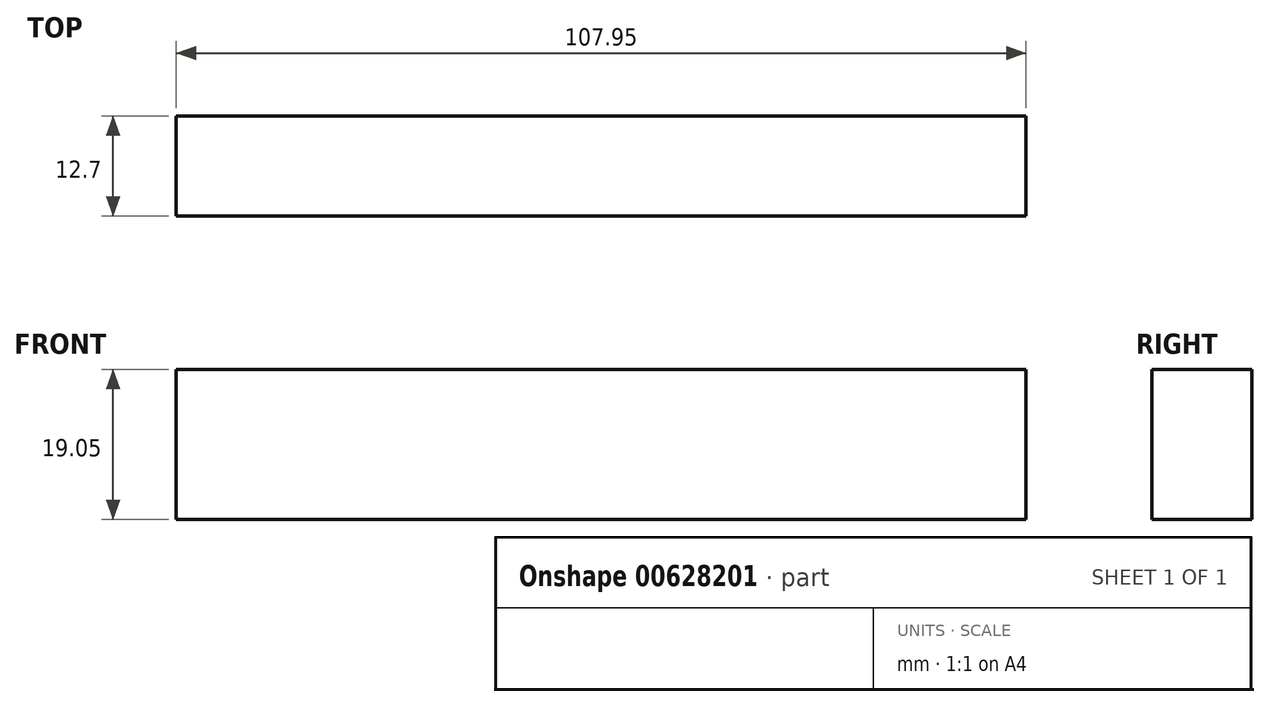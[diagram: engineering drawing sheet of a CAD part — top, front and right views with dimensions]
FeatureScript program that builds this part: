
annotation { "Feature Type Name" : "Feature", "Feature Type Description" : "" }
export const myFeature = defineFeature(function(context is Context, id is Id, definition is map)
    precondition{}
    {
        {
            var Q0;
            Q0=qCreatedBy(makeId("Front.planeOp"),FACE);
            var sketch = newSketch(context, id + "F0", { "sketchPlane" : qUnion([Q0])});
            skLineSegment(sketch, "E0.bottom", {"start": v(0, 0) * mm, "end": v(107.95, 0) * mm});
            skLineSegment(sketch, "E0.top", {"start": v(0, 19.05) * mm, "end": v(107.95, 19.05) * mm});
            skLineSegment(sketch, "E0.left", {"start": v(0, 0) * mm, "end": v(0, 19.05) * mm});
            skLineSegment(sketch, "E0.right", {"start": v(107.95, 0) * mm, "end": v(107.95, 19.05) * mm});
            skSolve(sketch);
        }
        {
            var Q0;
            Q0=qSketchRegion(id+"F0",true);
            extrude(context, id + "F1", {"entities" : qUnion([Q0]), "depth" : 12.7 * mm, "offsetDistance" : 25.4 * mm});
        }
    });
